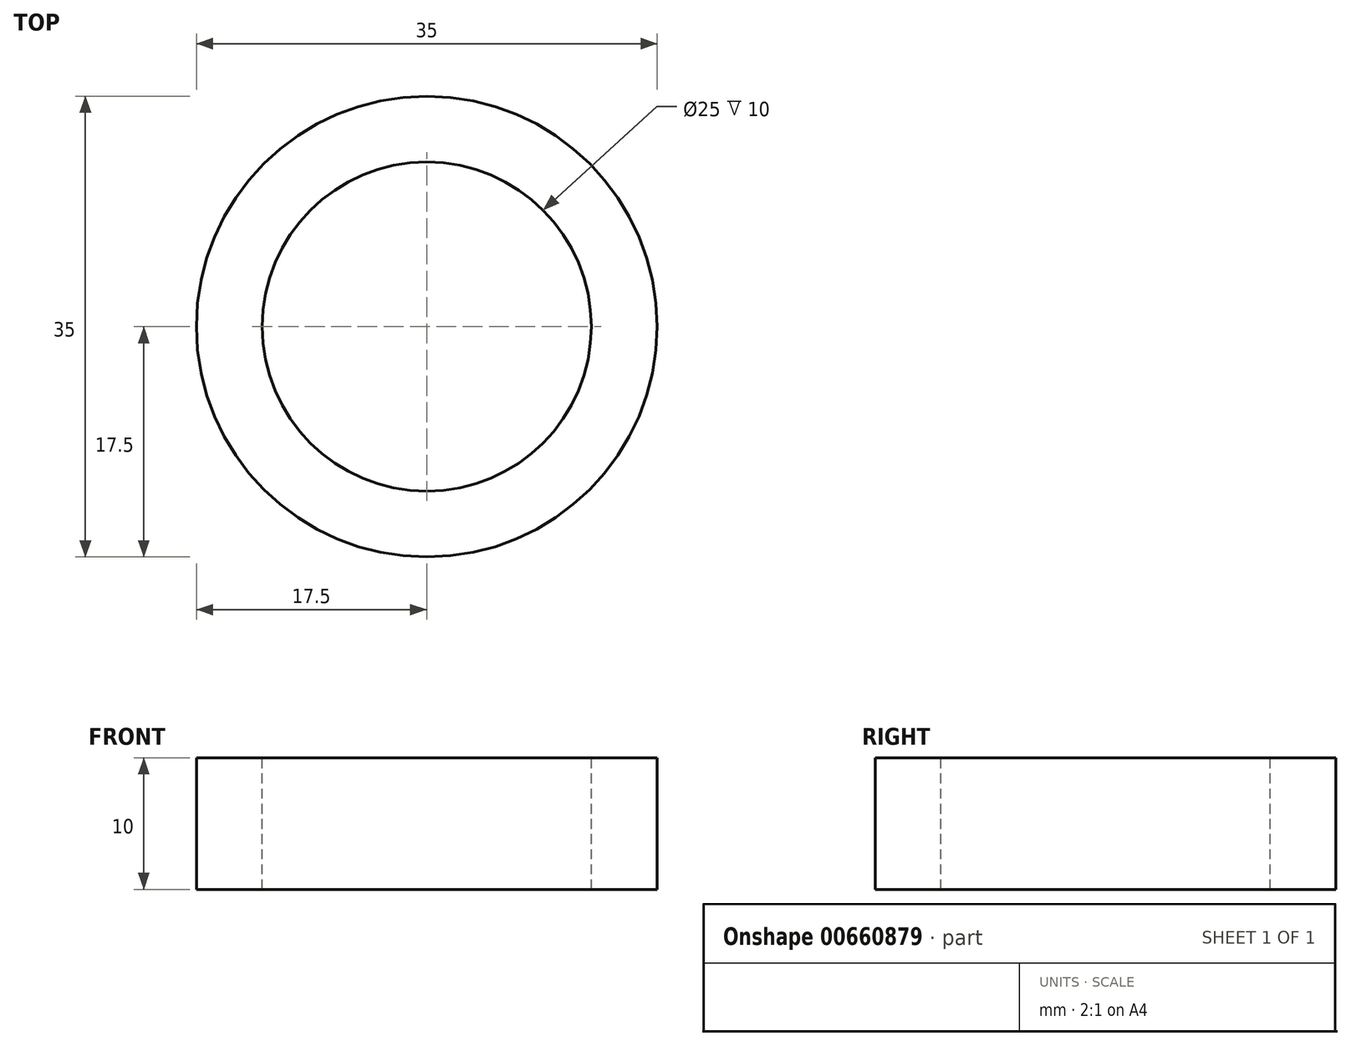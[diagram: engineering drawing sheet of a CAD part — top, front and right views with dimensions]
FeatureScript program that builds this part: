
annotation { "Feature Type Name" : "Feature", "Feature Type Description" : "" }
export const myFeature = defineFeature(function(context is Context, id is Id, definition is map)
    precondition{}
    {
        {
            var Q0;
            Q0=qCreatedBy(makeId("Top.planeOp"),FACE);
            var sketch = newSketch(context, id + "F0", { "sketchPlane" : qUnion([Q0])});
            skCircle(sketch, "E0", {"center": v(0, 0) * mm, "radius": 12.5 * mm});
            skCircle(sketch, "E1.0", {"center": v(0, 0) * mm, "radius": 17.5 * mm});
            skSolve(sketch);
        }
        {
            var Q0;
            Q0=makeQuery(id+"F0.imprint","IMPRINT",FACE,{"disambiguationData":[TD([[makeQuery(id+"F0.imprint","IMPRINT",EDGE,{"derivedFrom":sQuery(id+"F0.wireOp",EDGE,"E0")}),-1.0]])]});
            extrude(context, id + "F1", {"entities" : qUnion([Q0]), "oppositeDirection" : true, "depth" : 5 * mm, "offsetDistance" : 25 * mm});
        }
        {
            var Q0;
            Q0=makeQuery(id+"F1.opExtrude","CAP_FACE",FACE,{"disambiguationData":[OSD([sQuery(id+"F0.wireOp",EDGE,"E0"),sQuery(id+"F0.wireOp",EDGE,"E1.0")])],"isStart":false});
            var sketch = newSketch(context, id + "F2", { "sketchPlane" : qUnion([Q0])});
            skSolve(sketch);
        }
        {
            var Q0;
            Q0=makeQuery(id+"F2.imprint","IMPRINT",FACE,{"disambiguationData":[TD([[makeQuery(id+"F2.imprint","IMPRINT",EDGE,{"derivedFrom":makeQuery(id+"F1.opExtrude","CAP_EDGE",EDGE,{"disambiguationData":[OSD([sQuery(id+"F0.wireOp",EDGE,"E0")])],"isStart":false})}),1.0]])]});
            extrude(context, id + "F3", {"entities" : qUnion([Q0]), "operationType" : NewBodyOperationType.ADD, "depth" : 5 * mm, "offsetDistance" : 25 * mm});
        }
    });
